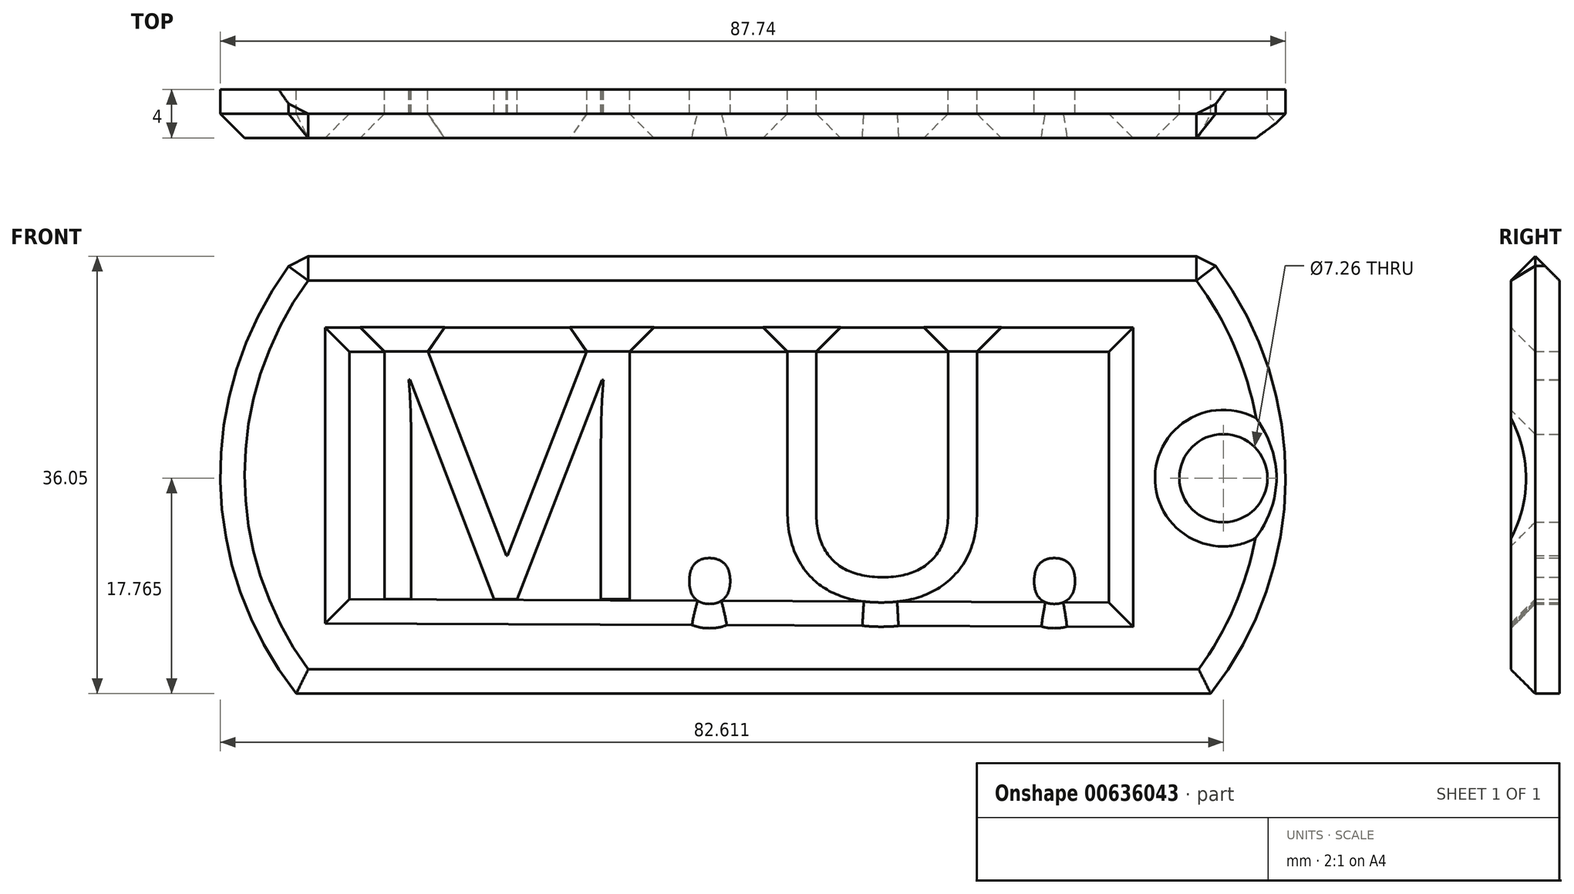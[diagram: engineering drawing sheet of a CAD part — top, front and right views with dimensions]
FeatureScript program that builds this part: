
annotation { "Feature Type Name" : "Feature", "Feature Type Description" : "" }
export const myFeature = defineFeature(function(context is Context, id is Id, definition is map)
    precondition{}
    {
        {
            var Q0;
            Q0=qCreatedBy(makeId("Front.planeOp"),FACE);
            var sketch = newSketch(context, id + "F0", { "sketchPlane" : qUnion([Q0])});
            skLineSegment(sketch, "E0", {"start": v(0, 0) * mm, "end": v(75.32, 0) * mm});
            skArc(sketch, "E1", {"start": v(0, 36.05) * mm, "mid": v(-6.25, 18.03) * mm, "end": v(0, 0) * mm});
            skLineSegment(sketch, "E2", {"start": v(0, 36.05) * mm, "end": v(75.11, 36.05) * mm});
            skArc(sketch, "E3", {"start": v(75.32, 0) * mm, "mid": v(81.49, 18.06) * mm, "end": v(75.11, 36.05) * mm});
            skCircle(sketch, "E4", {"center": v(76.36, 17.77) * mm, "radius": 3.63 * mm});
            skText(sketch, "E5", { "text": "M.U.", "fontName": "OpenSans-Regular.ttf"});
            const initialGuessF0  = {"E5": [0.00447, 0.0078, 1, 0, 0.02057]};
            skSetInitialGuess(sketch, initialGuessF0);
            skSolve(sketch);
        }
        {
            var Q0;
            Q0 = qSketchRegion(id + "F0", true);
            extrude(context, id + "F1", {"entities" : qUnion([Q0]), "endBound" : BoundingType.SYMMETRIC, "depth" : 2 * mm, "offsetDistance" : 25 * mm});
        }
        {
            var Q0;
            Q0=makeQuery(id+"F1.opExtrude","CAP_FACE",FACE,{"disambiguationData":[OSD([sQuery(id+"F0.wireOp",EDGE,"E0"),sQuery(id+"F0.wireOp",EDGE,"E1"),sQuery(id+"F0.wireOp",EDGE,"E2"),sQuery(id+"F0.wireOp",EDGE,"E3"),sQuery(id+"F0.wireOp",EDGE,"E4"),sQuery(id+"F0.wireOp",EDGE,"E5.sketch_text.stroke-0"),sQuery(id+"F0.wireOp",EDGE,"E5.sketch_text.stroke-1"),sQuery(id+"F0.wireOp",EDGE,"E5.sketch_text.stroke-2"),sQuery(id+"F0.wireOp",EDGE,"E5.sketch_text.stroke-3"),sQuery(id+"F0.wireOp",EDGE,"E5.sketch_text.stroke-4"),sQuery(id+"F0.wireOp",EDGE,"E5.sketch_text.stroke-5"),sQuery(id+"F0.wireOp",EDGE,"E5.sketch_text.stroke-6"),sQuery(id+"F0.wireOp",EDGE,"E5.sketch_text.stroke-7"),sQuery(id+"F0.wireOp",EDGE,"E5.sketch_text.stroke-8"),sQuery(id+"F0.wireOp",EDGE,"E5.sketch_text.stroke-9"),sQuery(id+"F0.wireOp",EDGE,"E5.sketch_text.stroke-10"),sQuery(id+"F0.wireOp",EDGE,"E5.sketch_text.stroke-11"),sQuery(id+"F0.wireOp",EDGE,"E5.sketch_text.stroke-12"),sQuery(id+"F0.wireOp",EDGE,"E5.sketch_text.stroke-13"),sQuery(id+"F0.wireOp",EDGE,"E5.sketch_text.stroke-14"),sQuery(id+"F0.wireOp",EDGE,"E5.sketch_text.stroke-15"),sQuery(id+"F0.wireOp",EDGE,"E5.sketch_text.stroke-16"),sQuery(id+"F0.wireOp",EDGE,"E5.sketch_text.stroke-17"),sQuery(id+"F0.wireOp",EDGE,"E5.sketch_text.stroke-18"),sQuery(id+"F0.wireOp",EDGE,"E5.sketch_text.stroke-19"),sQuery(id+"F0.wireOp",EDGE,"E5.sketch_text.stroke-20"),sQuery(id+"F0.wireOp",EDGE,"E5.sketch_text.stroke-21"),sQuery(id+"F0.wireOp",EDGE,"E5.sketch_text.stroke-22"),sQuery(id+"F0.wireOp",EDGE,"E5.sketch_text.stroke-23"),sQuery(id+"F0.wireOp",EDGE,"E5.sketch_text.stroke-24"),sQuery(id+"F0.wireOp",EDGE,"E5.sketch_text.stroke-25"),sQuery(id+"F0.wireOp",EDGE,"E5.sketch_text.stroke-26"),sQuery(id+"F0.wireOp",EDGE,"E5.sketch_text.stroke-27"),sQuery(id+"F0.wireOp",EDGE,"E5.sketch_text.stroke-28"),sQuery(id+"F0.wireOp",EDGE,"E5.sketch_text.stroke-29"),sQuery(id+"F0.wireOp",EDGE,"E5.sketch_text.stroke-30"),sQuery(id+"F0.wireOp",EDGE,"E5.sketch_text.stroke-31"),sQuery(id+"F0.wireOp",EDGE,"E5.sketch_text.stroke-32"),sQuery(id+"F0.wireOp",EDGE,"E5.sketch_text.stroke-33"),sQuery(id+"F0.wireOp",EDGE,"E5.sketch_text.stroke-34"),sQuery(id+"F0.wireOp",EDGE,"E5.sketch_text.stroke-35"),sQuery(id+"F0.wireOp",EDGE,"E5.sketch_text.stroke-36"),sQuery(id+"F0.wireOp",EDGE,"E5.sketch_text.stroke-37"),sQuery(id+"F0.wireOp",EDGE,"E5.sketch_text.stroke-38"),sQuery(id+"F0.wireOp",EDGE,"E5.sketch_text.stroke-39"),sQuery(id+"F0.wireOp",EDGE,"E5.sketch_text.stroke-40"),sQuery(id+"F0.wireOp",EDGE,"E5.sketch_text.stroke-41"),sQuery(id+"F0.wireOp",EDGE,"E5.sketch_text.stroke-42"),sQuery(id+"F0.wireOp",EDGE,"E5.sketch_text.stroke-43"),sQuery(id+"F0.wireOp",EDGE,"E5.sketch_text.stroke-44"),sQuery(id+"F0.wireOp",EDGE,"E5.sketch_text.stroke-45"),sQuery(id+"F0.wireOp",EDGE,"E5.sketch_text.stroke-46"),sQuery(id+"F0.wireOp",EDGE,"E5.sketch_text.stroke-47")])],"isStart":false});
            var sketch = newSketch(context, id + "F2", { "sketchPlane" : qUnion([Q0])});
            skLineSegment(sketch, "E6", {"start": v(4.39, 28.19) * mm, "end": v(4.39, 7.8) * mm});
            skLineSegment(sketch, "E7", {"start": v(4.39, 7.8) * mm, "end": v(66.93, 7.51) * mm});
            skLineSegment(sketch, "E8", {"start": v(66.93, 7.51) * mm, "end": v(66.93, 28.19) * mm});
            skLineSegment(sketch, "E9", {"start": v(66.93, 28.19) * mm, "end": v(4.39, 28.19) * mm});
            skSolve(sketch);
        }
        {
            var Q0;
            {var subQ14=sQuery(id+"F2.wireOp",EDGE,"E6");Q0=makeQuery(id+"F2.imprint","IMPRINT",FACE,{"disambiguationData":[TD([[makeQuery(id+"F2.imprint","IMPRINT",EDGE,{"derivedFrom":subQ14}),-1.0]])]});}
            extrude(context, id + "F3", {"entities" : qUnion([Q0]), "operationType" : NewBodyOperationType.ADD, "depth" : 2 * mm, "offsetDistance" : 25 * mm});
        }
        {
            var Q0;
            Q0=makeQuery(id+"F3.opExtrude","CAP_EDGE",EDGE,{"disambiguationData":[OSD([sQuery(id+"F0.wireOp",EDGE,"E2")])],"isStart":false});
            var Q1;
            Q1=makeQuery(id+"F3.opExtrude","CAP_FACE",FACE,{"disambiguationData":[OSD([sQuery(id+"F0.wireOp",EDGE,"E0"),sQuery(id+"F0.wireOp",EDGE,"E1"),sQuery(id+"F0.wireOp",EDGE,"E2"),sQuery(id+"F0.wireOp",EDGE,"E3"),sQuery(id+"F0.wireOp",EDGE,"E4"),sQuery(id+"F0.wireOp",EDGE,"E5.sketch_text.stroke-23"),sQuery(id+"F0.wireOp",EDGE,"E5.sketch_text.stroke-24"),sQuery(id+"F0.wireOp",EDGE,"E5.sketch_text.stroke-28"),sQuery(id+"F0.wireOp",EDGE,"E5.sketch_text.stroke-29"),sQuery(id+"F0.wireOp",EDGE,"E5.sketch_text.stroke-45"),sQuery(id+"F0.wireOp",EDGE,"E5.sketch_text.stroke-46"),sQuery(id+"F2.wireOp",EDGE,"E6"),sQuery(id+"F2.wireOp",EDGE,"E7"),sQuery(id+"F2.wireOp",EDGE,"E8"),sQuery(id+"F2.wireOp",EDGE,"E9")])],"isStart":false});
            var Q2;
            {var subQ0=sQuery(id+"F0.wireOp",EDGE,"E2");Q2=makeQuery(id+"F3.boolean.opBoolean","MERGE",FACE,{"derivedFrom":[makeQuery(id+"F1.opExtrude","SWEPT_FACE",FACE,{"disambiguationData":[OSD([subQ0])]}),makeQuery(id+"F3.opExtrude","SWEPT_FACE",FACE,{"disambiguationData":[OSD([subQ0])]})]});}
            chamfer(context, id + "F4", {"entities" : qUnion([Q0, Q1, Q2]), "width" : 2 * mm, "tangentPropagation" : true});
        }
    });
